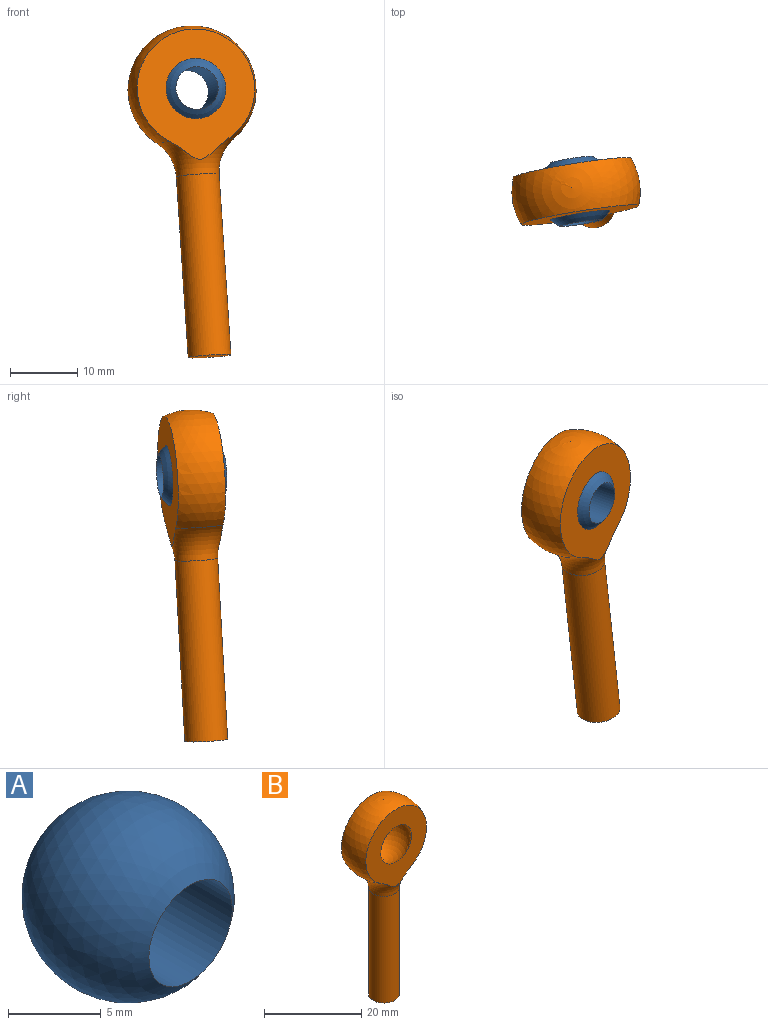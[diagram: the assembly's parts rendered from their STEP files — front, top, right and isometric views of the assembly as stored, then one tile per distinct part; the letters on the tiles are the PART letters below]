
ASSEMBLY  parts=2 mates=1
PART A: 2 faces, bbox 11.4x9.5x11.4 mm
  f0: sphere r=5.72mm, area 342.6mm2, adj f1
  f1: cylinder r=3.17mm len=9.53mm, axis (0,1,0), area 190mm2, adj f0
PART B: 7 faces, bbox 20.6x20.6x49.1 mm
  f0: torus R=9.53mm, axis (0,0,1), area 108.3mm2, adj f1,f2,f4,f5
  f1: sphere r=9.53mm, area 343.2mm2, adj f0,f4,f5
  f2: cylinder r=3.17mm len=26.92mm, axis (0,0,1), area 537.1mm2, adj f0,f3
  f3: plane 6.35x6.35mm, normal (0,0,-1), area 31.7mm2, adj f2
  f4: plane 19.37x17.67mm, normal (0,1,0), area 189mm2, adj f0,f1,f6
  f5: plane 19.37x17.67mm, normal (0,-1,0), area 189mm2, adj f0,f1,f6
  f6: sphere r=5.72mm, area 255.8mm2, adj f4,f5
PLACE A rot(axis=(-0.09,1,-0.01),144deg) t=(-1.51,-0.25,-0.09)mm
PLACE B rot(axis=(-0.33,-0.33,0.88),10.5deg) t=(-1.51,-0.25,-0.09)mm fixed
MATE ball B.f0 <-> A.f0  axis (-0.07,0.05,1) through (-1.51,-0.25,-0.09)mm
